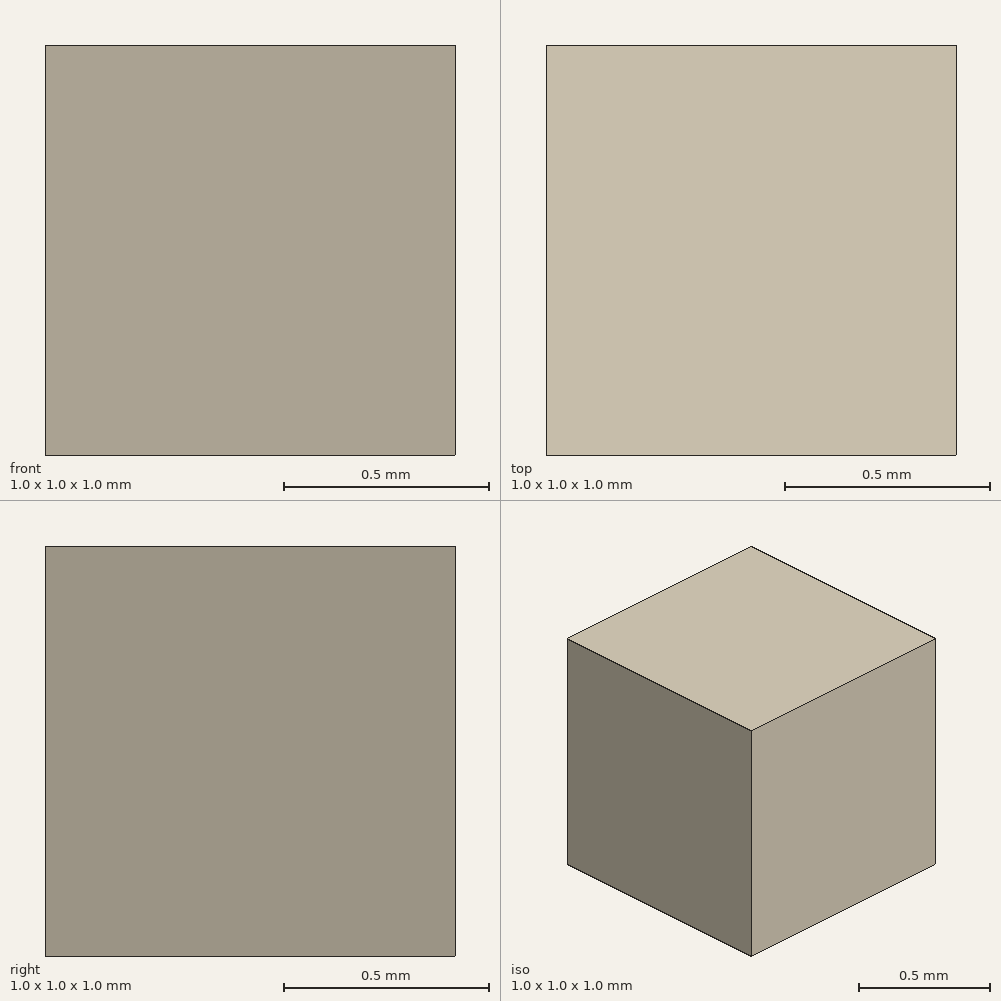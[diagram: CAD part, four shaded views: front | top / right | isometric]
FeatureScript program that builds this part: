
annotation { "Feature Type Name" : "Feature", "Feature Type Description" : "" }
export const myFeature = defineFeature(function(context is Context, id is Id, definition is map)
    precondition{}
    {
        {
            var Q0;
            Q0=qCreatedBy(makeId("Top.planeOp"),FACE);
            var sketch = newSketch(context, id + "F0", { "sketchPlane" : qUnion([Q0])});
            skLineSegment(sketch, "E0.bottom", {"start": v(0.5, -0.5) * mm, "end": v(-0.5, -0.5) * mm});
            skLineSegment(sketch, "E0.top", {"start": v(0.5, 0.5) * mm, "end": v(-0.5, 0.5) * mm});
            skLineSegment(sketch, "E0.left", {"start": v(0.5, -0.5) * mm, "end": v(0.5, 0.5) * mm});
            skLineSegment(sketch, "E0.right", {"start": v(-0.5, -0.5) * mm, "end": v(-0.5, 0.5) * mm});
            skPoint(sketch, "E0.middle", {"position": v(0, 0) * mm});
            skSolve(sketch);
        }
        {
            var Q0;
            Q0 = qSketchRegion(id + "F0", true);
            extrude(context, id + "F1", {"entities" : qUnion([Q0]), "depth" : 1 * mm});
        }
    });
